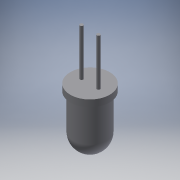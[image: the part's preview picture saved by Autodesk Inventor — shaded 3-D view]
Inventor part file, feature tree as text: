
AUTODESK INVENTOR PART (.ipt)
format: ipt  version: 2018 (Build 220112000, 112)  size: 124,928 bytes
history: native  units: mm
features: sketch x2, revolve x1, extrude x1
ambient origin geometry x8: Origin, YZ Plane, XZ Plane, XY Plane, X Axis, Y Axis, Z Axis, Center Point
bodies: Solid1 (feature_tree)
feature tree (4):
  revolve  "Revolution1"  [1 undecoded]
  extrude  "Extrusion1"  Depth=5.0mm
  sketch  "Sketch1"  dims[d0=8.7mm d1=5.9mm]
  sketch  "Sketch2"  dims[d2=1.0mm d3=5.0mm d4=90.0deg d5=2.54mm d6=1.27mm d7=0.5mm d8=0.5mm d9=4.0mm d10=0.0mm]
note: 1 required parameter value undecoded (feature->parameter linkage not recoverable at this tier; creation-order binding heuristic only, values carry confidence <= 0.55)
